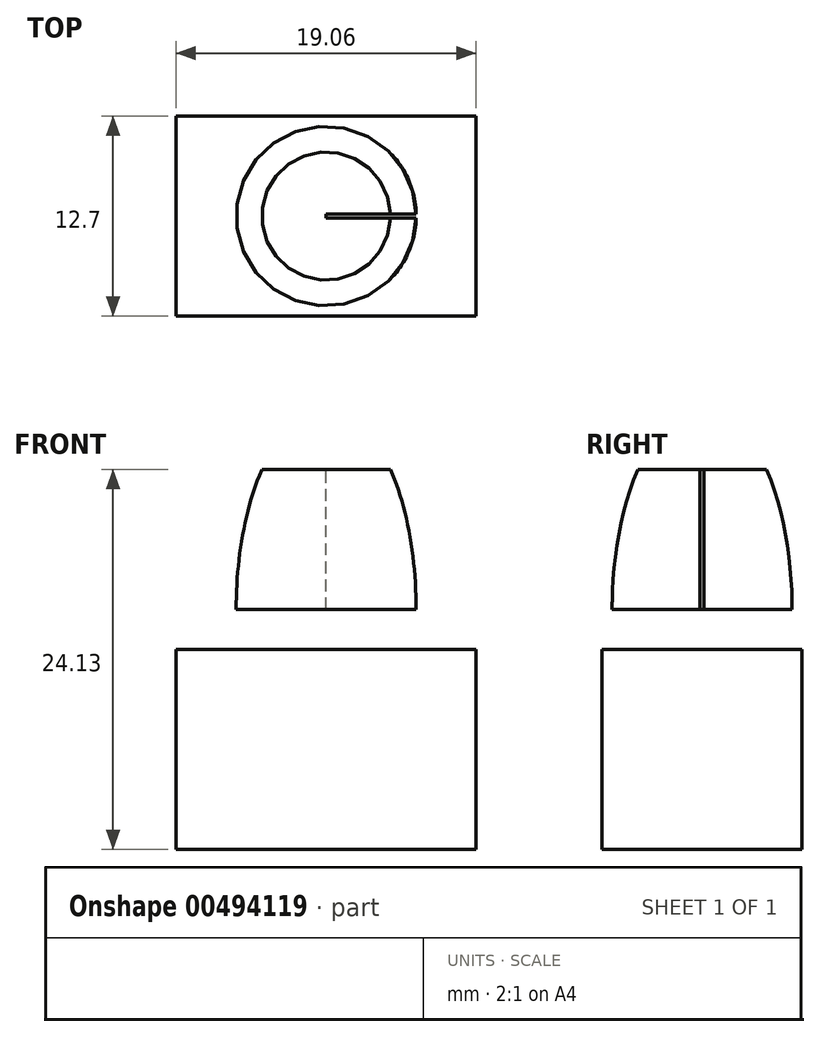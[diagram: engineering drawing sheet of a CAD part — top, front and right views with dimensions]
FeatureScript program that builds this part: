
annotation { "Feature Type Name" : "Feature", "Feature Type Description" : "" }
export const myFeature = defineFeature(function(context is Context, id is Id, definition is map)
    precondition{}
    {
        {
            var Q0;
            Q0=qCreatedBy(makeId("Top.planeOp"),FACE);
            var sketch = newSketch(context, id + "F0", { "sketchPlane" : qUnion([Q0])});
            skLineSegment(sketch, "E0.bottom", {"start": v(-9.2, 6.35) * mm, "end": v(9.2, 6.35) * mm});
            skLineSegment(sketch, "E0.top", {"start": v(-9.2, -6.35) * mm, "end": v(9.2, -6.35) * mm});
            skLineSegment(sketch, "E0.left", {"start": v(-9.53, 6.03) * mm, "end": v(-9.53, -6.03) * mm});
            skLineSegment(sketch, "E0.right", {"start": v(9.53, 6.03) * mm, "end": v(9.52, -6.03) * mm});
            skPoint(sketch, "E0.middle", {"position": v(0, 0) * mm});
            skPoint(sketch, "E1.visualSharp", {"position": v(-9.52, 6.35) * mm});
            skArc(sketch, "E1.filletArc", {"start": v(-9.2, 6.35) * mm, "mid": v(-9.43, 6.26) * mm, "end": v(-9.52, 6.03) * mm});
            skPoint(sketch, "E2.visualSharp", {"position": v(-9.53, -6.35) * mm});
            skArc(sketch, "E2.filletArc", {"start": v(-9.53, -6.03) * mm, "mid": v(-9.43, -6.26) * mm, "end": v(-9.2, -6.35) * mm});
            skPoint(sketch, "E3.visualSharp", {"position": v(9.52, -6.35) * mm});
            skArc(sketch, "E3.filletArc", {"start": v(9.2, -6.35) * mm, "mid": v(9.43, -6.26) * mm, "end": v(9.52, -6.03) * mm});
            skPoint(sketch, "E4.visualSharp", {"position": v(9.52, 6.35) * mm});
            skArc(sketch, "E4.filletArc", {"start": v(9.53, 6.03) * mm, "mid": v(9.43, 6.26) * mm, "end": v(9.2, 6.35) * mm});
            skLineSegment(sketch, "E5", {"start": v(-9.53, 6.03) * mm, "end": v(-9.53, 6.35) * mm});
            skLineSegment(sketch, "E6", {"start": v(-9.2, 6.35) * mm, "end": v(-9.52, 6.35) * mm});
            skLineSegment(sketch, "E7", {"start": v(9.2, 6.35) * mm, "end": v(9.52, 6.35) * mm});
            skLineSegment(sketch, "E8", {"start": v(9.53, 6.35) * mm, "end": v(9.53, 6.03) * mm});
            skLineSegment(sketch, "E9", {"start": v(9.52, -6.03) * mm, "end": v(9.52, -6.35) * mm});
            skLineSegment(sketch, "E10", {"start": v(9.52, -6.35) * mm, "end": v(9.2, -6.35) * mm});
            skLineSegment(sketch, "E11", {"start": v(-9.53, -6.03) * mm, "end": v(-9.53, -6.35) * mm});
            skLineSegment(sketch, "E12", {"start": v(-9.53, -6.35) * mm, "end": v(-9.2, -6.35) * mm});
            skSolve(sketch);
        }
        {
            var Q0;
            Q0 = qSketchRegion(id + "F0", true);
            extrude(context, id + "F1", {"entities" : qUnion([Q0]), "endBound" : BoundingType.SYMMETRIC, "depth" : 12.7 * mm});
        }
        {
            var Q0;
            Q0=makeQuery(id+"F1.opExtrude","SWEPT_FACE",FACE,{"disambiguationData":[OSD([sQuery(id+"F0.wireOp",EDGE,"E0.top")])]});
            var sketch = newSketch(context, id + "F2", { "sketchPlane" : qUnion([Q0])});
            skLineSegment(sketch, "E13", {"start": v(-9.53, -6.35) * mm, "end": v(-3.18, -6.35) * mm});
            skLineSegment(sketch, "E14", {"start": v(-3.18, -6.35) * mm, "end": v(3.17, -6.35) * mm});
            skLineSegment(sketch, "E15", {"start": v(3.17, -6.35) * mm, "end": v(9.52, -6.35) * mm});
            skLineSegment(sketch, "E16", {"start": v(-3.18, -6.35) * mm, "end": v(-3.18, 0) * mm});
            skLineSegment(sketch, "E17", {"start": v(-3.18, 0) * mm, "end": v(-9.53, 0) * mm});
            skLineSegment(sketch, "E18", {"start": v(3.17, -6.35) * mm, "end": v(3.17, 0) * mm});
            skLineSegment(sketch, "E19", {"start": v(3.17, 0) * mm, "end": v(-3.18, 0) * mm});
            skLineSegment(sketch, "E20", {"start": v(3.17, 0) * mm, "end": v(9.52, 0) * mm});
            skLineSegment(sketch, "E21", {"start": v(-3.18, 0) * mm, "end": v(-3.18, 6.35) * mm});
            skLineSegment(sketch, "E22", {"start": v(3.17, 0) * mm, "end": v(3.17, 6.35) * mm});
            skSolve(sketch);
        }
        {
            var Q0;
            Q0=makeQuery(id+"F1.opExtrude","SWEPT_FACE",FACE,{"disambiguationData":[OSD([sQuery(id+"F0.wireOp",EDGE,"E0.bottom"),sQuery(id+"F0.wireOp",EDGE,"E6"),sQuery(id+"F0.wireOp",EDGE,"E7")])]});
            var sketch = newSketch(context, id + "F3", { "sketchPlane" : qUnion([Q0])});
            skLineSegment(sketch, "E23", {"start": v(-9.53, -6.35) * mm, "end": v(-3.17, -6.35) * mm});
            skLineSegment(sketch, "E24", {"start": v(-3.17, -6.35) * mm, "end": v(3.18, -6.35) * mm});
            skLineSegment(sketch, "E25", {"start": v(3.18, -6.35) * mm, "end": v(9.53, -6.35) * mm});
            skLineSegment(sketch, "E26", {"start": v(-3.17, -6.35) * mm, "end": v(-3.17, 0) * mm});
            skLineSegment(sketch, "E27", {"start": v(-3.17, 0) * mm, "end": v(-9.53, 0) * mm});
            skLineSegment(sketch, "E28", {"start": v(-3.17, 0) * mm, "end": v(3.17, 0) * mm});
            skLineSegment(sketch, "E29", {"start": v(3.17, 0) * mm, "end": v(3.18, -6.35) * mm});
            skLineSegment(sketch, "E30", {"start": v(3.17, 0) * mm, "end": v(9.53, 0) * mm});
            skLineSegment(sketch, "E31", {"start": v(3.17, 0) * mm, "end": v(3.17, 6.35) * mm});
            skLineSegment(sketch, "E32", {"start": v(-3.17, 0) * mm, "end": v(-3.17, 6.35) * mm});
            skSolve(sketch);
        }
        {
            var Q0;
            Q0=makeQuery(id+"F1.opExtrude","CAP_FACE",FACE,{"disambiguationData":[OSD([sQuery(id+"F0.wireOp",EDGE,"E0.bottom"),sQuery(id+"F0.wireOp",EDGE,"E0.top"),sQuery(id+"F0.wireOp",EDGE,"E0.left"),sQuery(id+"F0.wireOp",EDGE,"E0.right"),sQuery(id+"F0.wireOp",EDGE,"E5"),sQuery(id+"F0.wireOp",EDGE,"E6"),sQuery(id+"F0.wireOp",EDGE,"E7"),sQuery(id+"F0.wireOp",EDGE,"E8"),sQuery(id+"F0.wireOp",EDGE,"E9"),sQuery(id+"F0.wireOp",EDGE,"E10"),sQuery(id+"F0.wireOp",EDGE,"E11"),sQuery(id+"F0.wireOp",EDGE,"E12")])],"isStart":true});
            var sketch = newSketch(context, id + "F4", { "sketchPlane" : qUnion([Q0])});
            skLineSegment(sketch, "E33", {"start": v(-9.53, -6.35) * mm, "end": v(-3.17, -6.35) * mm});
            skLineSegment(sketch, "E34", {"start": v(-3.17, -6.35) * mm, "end": v(3.18, -6.35) * mm});
            skLineSegment(sketch, "E35", {"start": v(3.18, -6.35) * mm, "end": v(9.53, -6.35) * mm});
            skLineSegment(sketch, "E36", {"start": v(-3.17, -6.35) * mm, "end": v(-3.17, 0) * mm});
            skLineSegment(sketch, "E37", {"start": v(-3.17, 0) * mm, "end": v(-3.18, 6.35) * mm});
            skLineSegment(sketch, "E38", {"start": v(-9.53, 0) * mm, "end": v(-3.17, 0) * mm});
            skLineSegment(sketch, "E39", {"start": v(-3.17, 0) * mm, "end": v(3.17, 0) * mm});
            skLineSegment(sketch, "E40", {"start": v(3.17, 0) * mm, "end": v(9.52, 0) * mm});
            skLineSegment(sketch, "E41", {"start": v(3.18, -6.35) * mm, "end": v(3.17, 0) * mm});
            skLineSegment(sketch, "E42", {"start": v(3.17, 0) * mm, "end": v(3.17, 6.35) * mm});
            skSolve(sketch);
        }
        {
            var Q0;
            Q0=makeQuery(id+"F1.opExtrude","SWEPT_FACE",FACE,{"disambiguationData":[OSD([sQuery(id+"F0.wireOp",EDGE,"E0.right"),sQuery(id+"F0.wireOp",EDGE,"E8"),sQuery(id+"F0.wireOp",EDGE,"E9")])]});
            var sketch = newSketch(context, id + "F5", { "sketchPlane" : qUnion([Q0])});
            skLineSegment(sketch, "E43", {"start": v(-6.35, -6.35) * mm, "end": v(0, -6.35) * mm});
            skLineSegment(sketch, "E44", {"start": v(0, -6.35) * mm, "end": v(0, 0) * mm});
            skLineSegment(sketch, "E45", {"start": v(0, 0) * mm, "end": v(-6.35, 0) * mm});
            skLineSegment(sketch, "E46", {"start": v(0, 0) * mm, "end": v(0, 6.35) * mm});
            skLineSegment(sketch, "E47", {"start": v(0, 0) * mm, "end": v(6.35, 0) * mm});
            skSolve(sketch);
        }
        {
            var Q0;
            Q0=makeQuery(id+"F1.opExtrude","SWEPT_FACE",FACE,{"disambiguationData":[OSD([sQuery(id+"F0.wireOp",EDGE,"E0.left"),sQuery(id+"F0.wireOp",EDGE,"E5"),sQuery(id+"F0.wireOp",EDGE,"E11")])]});
            var sketch = newSketch(context, id + "F6", { "sketchPlane" : qUnion([Q0])});
            skLineSegment(sketch, "E48", {"start": v(-6.35, -6.35) * mm, "end": v(0, -6.35) * mm});
            skLineSegment(sketch, "E49", {"start": v(0, -6.35) * mm, "end": v(0, 0) * mm});
            skLineSegment(sketch, "E50", {"start": v(0, 0) * mm, "end": v(-6.35, 0) * mm});
            skLineSegment(sketch, "E51", {"start": v(0, 0) * mm, "end": v(0, 6.35) * mm});
            skLineSegment(sketch, "E52", {"start": v(0, 0) * mm, "end": v(6.35, 0) * mm});
            skSolve(sketch);
        }
        {
            var Q0;
            Q0=qCreatedBy(makeId("Front.planeOp"),FACE);
            var sketch = newSketch(context, id + "F7", { "sketchPlane" : qUnion([Q0])});
            skLineSegment(sketch, "E53.0.0", {"start": v(-9.53, -6.35) * mm, "end": v(-9.53, 6.03) * mm});
            skLineSegment(sketch, "E53.0.2", {"start": v(-9.52, 6.03) * mm, "end": v(-9.52, -6.35) * mm});
            skLineSegment(sketch, "E54.0.0", {"start": v(9.53, -6.35) * mm, "end": v(9.53, 6.03) * mm});
            skLineSegment(sketch, "E54.0.2", {"start": v(9.52, 6.03) * mm, "end": v(9.52, -6.35) * mm});
            skLineSegment(sketch, "E55.0.1", {"start": v(9.2, 6.35) * mm, "end": v(-9.2, 6.35) * mm});
            skLineSegment(sketch, "E55.0.3", {"start": v(-9.2, 6.35) * mm, "end": v(9.2, 6.35) * mm});
            skArc(sketch, "E56.0.0", {"start": v(9.2, 6.35) * mm, "mid": v(9.43, 6.26) * mm, "end": v(9.53, 6.03) * mm});
            skArc(sketch, "E56.0.2", {"start": v(9.53, 6.03) * mm, "mid": v(9.43, 6.26) * mm, "end": v(9.2, 6.35) * mm});
            skArc(sketch, "E57.0.0", {"start": v(-9.53, 6.03) * mm, "mid": v(-9.43, 6.26) * mm, "end": v(-9.2, 6.35) * mm});
            skArc(sketch, "E57.0.2", {"start": v(-9.2, 6.35) * mm, "mid": v(-9.43, 6.26) * mm, "end": v(-9.53, 6.03) * mm});
            skLineSegment(sketch, "E58.0.0", {"start": v(-9.2, -6.35) * mm, "end": v(-9.53, -6.35) * mm});
            skLineSegment(sketch, "E58.0.2", {"start": v(-9.52, -6.35) * mm, "end": v(-9.2, -6.35) * mm});
            skLineSegment(sketch, "E58.0.3", {"start": v(-9.2, -6.35) * mm, "end": v(9.2, -6.35) * mm});
            skLineSegment(sketch, "E58.0.4", {"start": v(9.2, -6.35) * mm, "end": v(9.53, -6.35) * mm});
            skLineSegment(sketch, "E58.0.6", {"start": v(9.52, -6.35) * mm, "end": v(9.2, -6.35) * mm});
            skLineSegment(sketch, "E58.0.7", {"start": v(9.2, -6.35) * mm, "end": v(-9.2, -6.35) * mm});
            skLineSegment(sketch, "E59.bottom", {"start": v(0, 6.35) * mm, "end": v(5.72, 6.35) * mm});
            skLineSegment(sketch, "E59.top", {"start": v(0, 8.9) * mm, "end": v(5.72, 8.9) * mm});
            skLineSegment(sketch, "E59.left", {"start": v(0, 6.35) * mm, "end": v(0, 8.9) * mm});
            skLineSegment(sketch, "E59.right", {"start": v(5.72, 6.35) * mm, "end": v(5.72, 8.9) * mm});
            skLineSegment(sketch, "E60", {"start": v(0, 6.35) * mm, "end": v(0, 17.78) * mm});
            skEllipticalArc(sketch, "E61", {});
            skLineSegment(sketch, "E62", {"start": v(0, 17.78) * mm, "end": v(4.08, 17.78) * mm});
            skFitSpline(sketch, "E63.0", {"points": [v(0.8, 20.72) * mm, v(0, 20.88) * mm, v(-0.8, 20.72) * mm, v(-1.52, 20.24) * mm, v(-2.11, 19.62) * mm, v(-2.7, 18.85) * mm, v(-3.37, 17.62) * mm, v(-3.93, 16.09) * mm, v(-4.3, 14.7) * mm, v(-4.62, 13.25) * mm, v(-4.83, 11.7) * mm, v(-4.93, 10.1) * mm, v(-4.96, 8.9) * mm, v(-4.93, 7.67) * mm, v(-4.83, 6.07) * mm, v(-4.62, 4.53) * mm, v(-4.3, 3.07) * mm, v(-3.93, 1.7) * mm, v(-3.37, 0.16) * mm, v(-2.7, -1.07) * mm, v(-2.11, -1.84) * mm, v(-1.52, -2.46) * mm, v(-0.8, -2.94) * mm, v(0, -3.1) * mm, v(0.8, -2.94) * mm, v(1.52, -2.46) * mm, v(2.11, -1.84) * mm, v(2.7, -1.07) * mm, v(3.37, 0.16) * mm, v(3.93, 1.7) * mm, v(4.3, 3.07) * mm, v(4.62, 4.53) * mm, v(4.83, 6.07) * mm, v(4.93, 7.67) * mm, v(4.96, 8.89) * mm, v(4.93, 10.1) * mm, v(4.83, 11.7) * mm, v(4.62, 13.25) * mm, v(4.3, 14.7) * mm, v(3.93, 16.09) * mm, v(3.37, 17.62) * mm, v(2.7, 18.85) * mm, v(2.11, 19.62) * mm, v(1.52, 20.24) * mm, v(0.8, 20.72) * mm, v(0, 20.88) * mm, v(-0.8, 20.72) * mm]});
            skLineSegment(sketch, "E64", {"start": v(3.38, 17.47) * mm, "end": v(3.38, 17.78) * mm});
            skFitSpline(sketch, "E65.0", {"points": [v(1.01, 21.19) * mm, v(0, 21.4) * mm, v(-1.01, 21.19) * mm, v(-1.85, 20.63) * mm, v(-2.5, 19.95) * mm, v(-3.13, 19.11) * mm, v(-3.83, 17.82) * mm, v(-4.42, 16.24) * mm, v(-4.8, 14.82) * mm, v(-5.12, 13.34) * mm, v(-5.33, 11.76) * mm, v(-5.44, 10.13) * mm, v(-5.47, 8.9) * mm, v(-5.44, 7.65) * mm, v(-5.33, 6.02) * mm, v(-5.12, 4.44) * mm, v(-4.8, 2.96) * mm, v(-4.42, 1.54) * mm, v(-3.83, -0.04) * mm, v(-3.13, -1.33) * mm, v(-2.5, -2.17) * mm, v(-1.85, -2.85) * mm, v(-1.01, -3.4) * mm, v(0, -3.63) * mm, v(1.01, -3.4) * mm, v(1.85, -2.85) * mm, v(2.5, -2.17) * mm, v(3.13, -1.33) * mm, v(3.83, -0.04) * mm, v(4.42, 1.54) * mm, v(4.8, 2.96) * mm, v(5.12, 4.44) * mm, v(5.33, 6.02) * mm, v(5.44, 7.65) * mm, v(5.47, 8.89) * mm, v(5.44, 10.13) * mm, v(5.33, 11.76) * mm, v(5.12, 13.34) * mm, v(4.8, 14.82) * mm, v(4.42, 16.24) * mm, v(3.83, 17.82) * mm, v(3.13, 19.11) * mm, v(2.5, 19.95) * mm, v(1.85, 20.63) * mm, v(1.01, 21.19) * mm, v(0, 21.4) * mm, v(-1.01, 21.19) * mm]});
            skLineSegment(sketch, "E66", {"start": v(3.85, 17.68) * mm, "end": v(3.82, 17.78) * mm});
            const initialGuessF7  = {"E61": [0, 0.00889, 0, 1, 0.0127, 0.005715, 4.71238898038469, 5.487786476995442]};
            skSetInitialGuess(sketch, initialGuessF7);
            skSolve(sketch);
        }
        {
            var Q0;
            Q0=makeQuery(id+"F7.imprint","IMPRINT",FACE,{"disambiguationData":[TD([[makeQuery(id+"F7.imprint","IMPRINT",EDGE,{"derivedFrom":sQuery(id+"F7.wireOp",EDGE,"E59.bottom")}),1.0]])]});
            var Q1;
            {var subQ0=sQuery(id+"F7.wireOp",EDGE,"65cb4639-48c5-4efa-a0bb-3e3d4f944c98.0");Q1=makeQuery(id+"F7.imprint","IMPRINT",FACE,{"disambiguationData":[TD([[makeQuery(id+"F7.imprint","IMPRINT",EDGE,{"derivedFrom":subQ0}),-1.0]])]});}
            var Q2;
            {var subQ1=sQuery(id+"F7.wireOp",EDGE,"UFTi9jcA-qrXZ-McEp-ELTr-vDtOSaNAptPX");Q2=makeQuery(id+"F7.imprint","IMPRINT",FACE,{"disambiguationData":[TD([[makeQuery(id+"F7.imprint","IMPRINT",EDGE,{"derivedFrom":subQ1}),1.0]])]});}
            var Q3;
            {var subQ0=sQuery(id+"F7.wireOp",EDGE,"E63.0");Q3=makeQuery(id+"F7.imprint","IMPRINT",FACE,{"disambiguationData":[TD([[makeQuery(id+"F7.imprint","IMPRINT",EDGE,{"derivedFrom":subQ0}),-1.0]])]});}
            var Q4;
            {var subQ1=sQuery(id+"F7.wireOp",EDGE,"E61");Q4=makeQuery(id+"F7.imprint","IMPRINT",FACE,{"disambiguationData":[TD([[makeQuery(id+"F7.imprint","IMPRINT",EDGE,{"derivedFrom":subQ1}),1.0]])]});}
            var Q5;
            Q5=sQuery(id+"F7.wireOp",EDGE,"E59.left");
            revolve(context, id + "F8", {"operationType" : NewBodyOperationType.ADD, "entities" : qUnion([Q0, Q1, Q2, Q3, Q4]), "axis" : qUnion([Q5]), "revolveType" : RevolveType.FULL});
        }
        {
            var Q0;
            {var subQ1=sQuery(id+"F7.wireOp",EDGE,"E61");Q0=makeQuery(id+"F7.imprint","IMPRINT",FACE,{"disambiguationData":[TD([[makeQuery(id+"F7.imprint","IMPRINT",EDGE,{"derivedFrom":subQ1}),1.0]])]});}
            extrude(context, id + "F9", {"entities" : qUnion([Q0]), "operationType" : NewBodyOperationType.REMOVE, "endBound" : BoundingType.SYMMETRIC, "depth" : 0.25 * mm});
        }
    });
